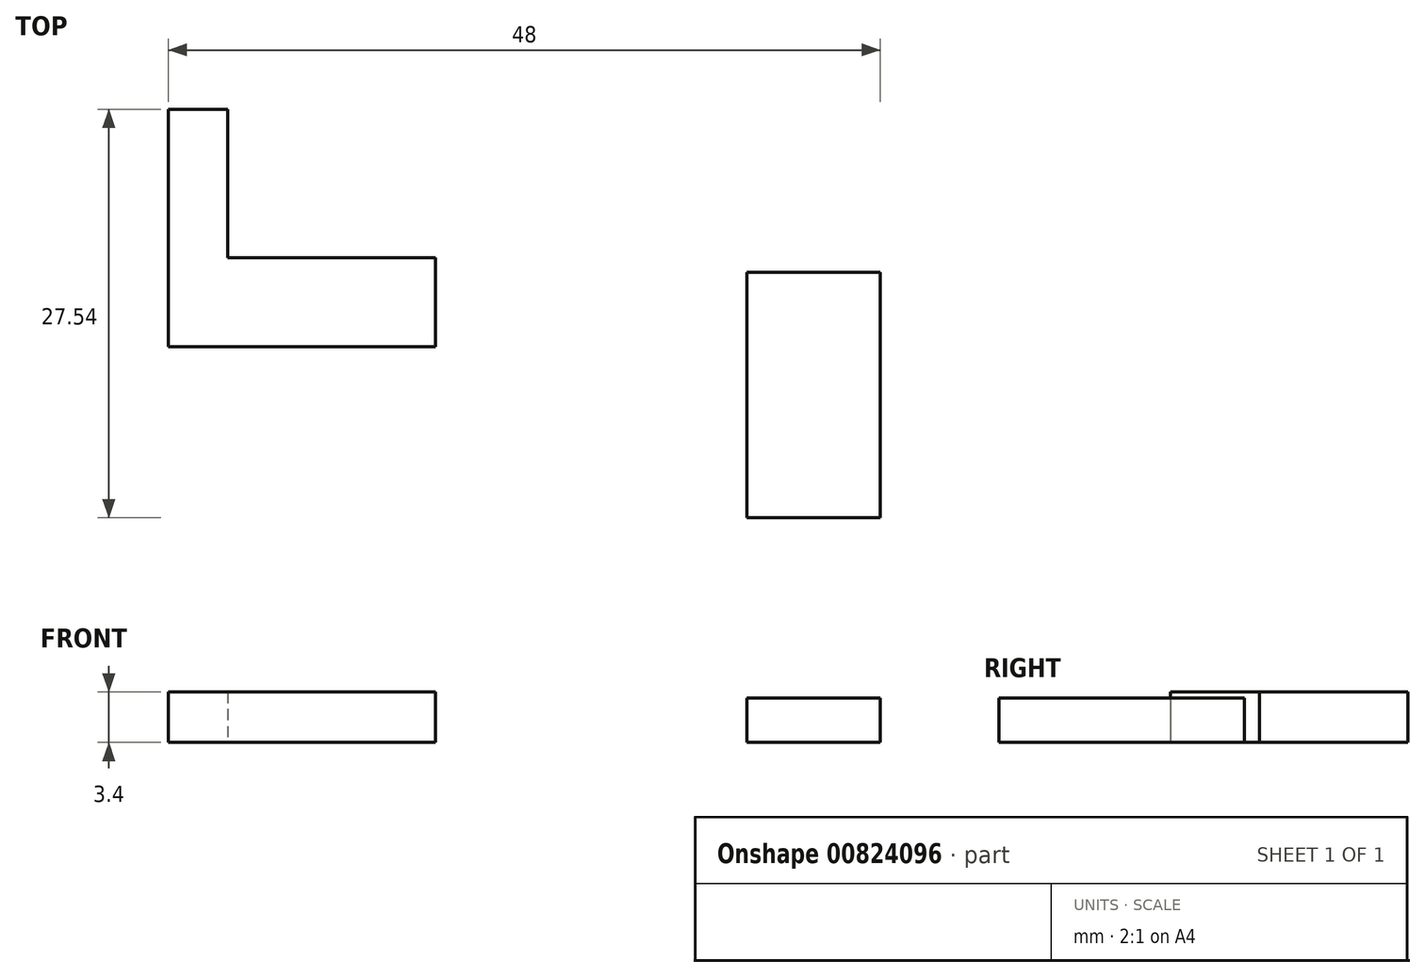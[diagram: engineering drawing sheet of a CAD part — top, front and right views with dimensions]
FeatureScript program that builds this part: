
annotation { "Feature Type Name" : "Feature", "Feature Type Description" : "" }
export const myFeature = defineFeature(function(context is Context, id is Id, definition is map)
    precondition{}
    {
        {
            var Q0;
            Q0=qCreatedBy(makeId("Top.planeOp"),FACE);
            var sketch = newSketch(context, id + "F0", { "sketchPlane" : qUnion([Q0])});
            skLineSegment(sketch, "E0.bottom", {"start": v(30, -20) * mm, "end": v(-30, -20) * mm});
            skLineSegment(sketch, "E0.top", {"start": v(30, 20) * mm, "end": v(-30, 20) * mm});
            skLineSegment(sketch, "E0.left", {"start": v(30, -20) * mm, "end": v(30, 20) * mm});
            skLineSegment(sketch, "E0.right", {"start": v(-30, -20) * mm, "end": v(-30, 20) * mm});
            skPoint(sketch, "E0.middle", {"position": v(0, 0) * mm});
            skLineSegment(sketch, "E1.bottom", {"start": v(-30, -20) * mm, "end": v(-12, -20) * mm});
            skLineSegment(sketch, "E1.left", {"start": v(-30, -20) * mm, "end": v(-30, -14) * mm});
            skLineSegment(sketch, "E2.left", {"start": v(-30, -14) * mm, "end": v(-30, 9) * mm});
            skLineSegment(sketch, "E3.bottom", {"start": v(-18, -6) * mm, "end": v(0, -6) * mm});
            skLineSegment(sketch, "E3.right", {"start": v(0, -6) * mm, "end": v(0, 0) * mm});
            skLineSegment(sketch, "E4", {"start": v(-18, 10) * mm, "end": v(-14, 10) * mm});
            skLineSegment(sketch, "E5", {"start": v(-14, 10) * mm, "end": v(-14, 0) * mm});
            skLineSegment(sketch, "E6", {"start": v(-18, -6) * mm, "end": v(-18, 10) * mm});
            skLineSegment(sketch, "E7", {"start": v(-14, 0) * mm, "end": v(0, 0) * mm});
            skLineSegment(sketch, "E8.bottom", {"start": v(30, -20) * mm, "end": v(21, -20) * mm});
            skLineSegment(sketch, "E8.top", {"start": v(30, -1) * mm, "end": v(21, -1) * mm});
            skLineSegment(sketch, "E8.left", {"start": v(30, -20) * mm, "end": v(30, -1) * mm});
            skLineSegment(sketch, "E8.right", {"start": v(21, -20) * mm, "end": v(21, -1) * mm});
            skLineSegment(sketch, "E9", {"start": v(21, -17.54) * mm, "end": v(30, -17.54) * mm});
            skLineSegment(sketch, "E10", {"start": v(30, -17.54) * mm, "end": v(21, -15.04) * mm});
            skSolve(sketch);
        }
        {
            var Q0;
            Q0=makeQuery(id+"F0.imprint","IMPRINT",FACE,{"disambiguationData":[TD([[makeQuery(id+"F0.imprint","IMPRINT",EDGE,{"derivedFrom":sQuery(id+"F0.wireOp",EDGE,"E3.bottom")}),1.0]])]});
            extrude(context, id + "F1", {"entities" : qUnion([Q0]), "depth" : 3.4 * mm, "offsetDistance" : 25 * mm});
        }
        {
            var Q0;
            {var subQ0=sQuery(id+"F0.wireOp",EDGE,"E8.top");Q0=makeQuery(id+"F0.imprint","IMPRINT",FACE,{"disambiguationData":[TD([[makeQuery(id+"F0.imprint","IMPRINT",EDGE,{"derivedFrom":subQ0}),1.0]])]});}
            extrude(context, id + "F2", {"entities" : qUnion([Q0]), "depth" : 3 * mm, "offsetDistance" : 25 * mm});
        }
        {
            var Q0;
            {var subQ0=sQuery(id+"F0.wireOp",EDGE,"E9");Q0=makeQuery(id+"F0.imprint","IMPRINT",FACE,{"disambiguationData":[TD([[makeQuery(id+"F0.imprint","IMPRINT",EDGE,{"derivedFrom":subQ0}),1.0]])]});}
            var Q1;
            {var subQ0=sQuery(id+"F0.wireOp",EDGE,"E8.bottom");Q1=makeQuery(id+"F0.imprint","IMPRINT",FACE,{"disambiguationData":[TD([[makeQuery(id+"F0.imprint","IMPRINT",EDGE,{"derivedFrom":subQ0}),-1.0]])]});}
            extrude(context, id + "F3", {"entities" : qUnion([Q0, Q1]), "operationType" : NewBodyOperationType.ADD, "depth" : 3 * mm, "offsetDistance" : 25 * mm});
        }
    });
